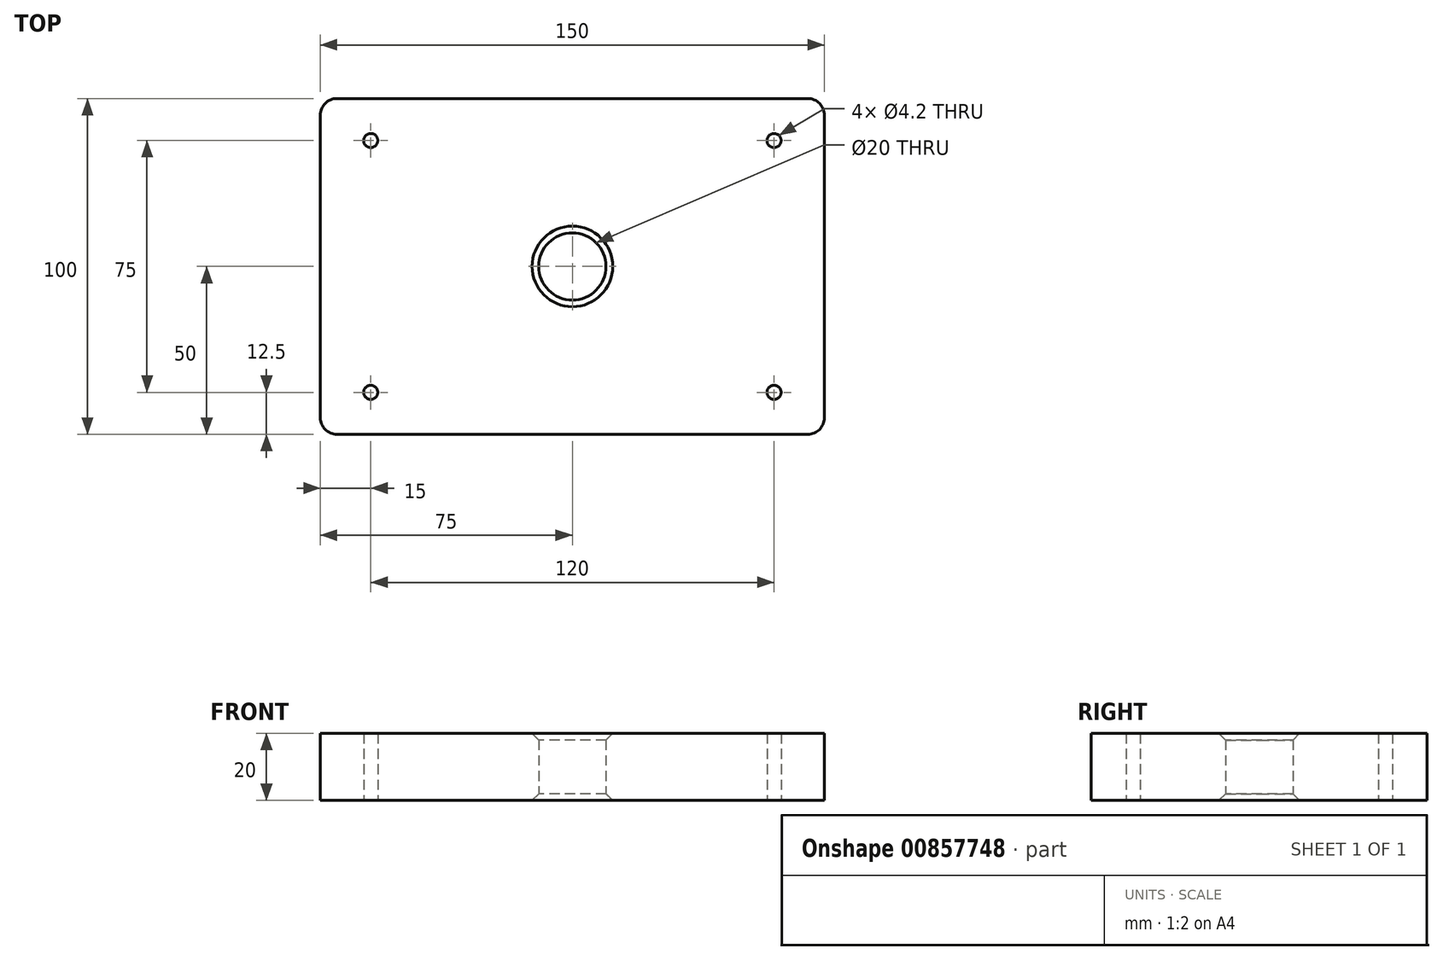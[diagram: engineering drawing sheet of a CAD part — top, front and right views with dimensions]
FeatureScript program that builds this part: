
annotation { "Feature Type Name" : "Feature", "Feature Type Description" : "" }
export const myFeature = defineFeature(function(context is Context, id is Id, definition is map)
    precondition{}
    {
        {
            var Q0;
            Q0=qCreatedBy(makeId("Top.planeOp"),FACE);
            var sketch = newSketch(context, id + "F0", { "sketchPlane" : qUnion([Q0])});
            skCircle(sketch, "E0", {"center": v(0, 0) * mm, "radius": 10 * mm});
            skLineSegment(sketch, "E1.bottom", {"start": v(-75, 50) * mm, "end": v(75, 50) * mm});
            skLineSegment(sketch, "E1.top", {"start": v(-75, -50) * mm, "end": v(75, -50) * mm});
            skLineSegment(sketch, "E1.left", {"start": v(-75, 50) * mm, "end": v(-75, -50) * mm});
            skLineSegment(sketch, "E1.right", {"start": v(75, 50) * mm, "end": v(75, -50) * mm});
            skLineSegment(sketch, "E2", {"start": v(-75, 50) * mm, "end": v(75, -50) * mm, "construction": true});
            skSolve(sketch);
        }
        {
            var Q0;
            Q0 = qSketchRegion(id + "F0", true);
            extrude(context, id + "F1", {"entities" : qUnion([Q0]), "depth" : 20 * mm, "offsetDistance" : 25.4 * mm});
        }
        {
            var Q0;
            Q0=makeQuery(id+"F1.opExtrude","SWEPT_EDGE",EDGE,{"disambiguationData":[OSD([sQuery(id+"F0.wireOp",EDGE,"E1.top"),sQuery(id+"F0.wireOp",EDGE,"E1.left")])]});
            var Q1;
            Q1=makeQuery(id+"F1.opExtrude","SWEPT_EDGE",EDGE,{"disambiguationData":[OSD([sQuery(id+"F0.wireOp",EDGE,"E1.bottom"),sQuery(id+"F0.wireOp",EDGE,"E1.left")])]});
            var Q2;
            Q2=makeQuery(id+"F1.opExtrude","SWEPT_EDGE",EDGE,{"disambiguationData":[OSD([sQuery(id+"F0.wireOp",EDGE,"E1.top"),sQuery(id+"F0.wireOp",EDGE,"E1.right")])]});
            var Q3;
            Q3=makeQuery(id+"F1.opExtrude","SWEPT_EDGE",EDGE,{"disambiguationData":[OSD([sQuery(id+"F0.wireOp",EDGE,"E1.bottom"),sQuery(id+"F0.wireOp",EDGE,"E1.right")])]});
            fillet(context, id + "F2", {"entities" : qUnion([Q0, Q1, Q2, Q3]), "radius" : 5 * mm, "tangentPropagation" : true, "allowEdgeOverflow" : false});
        }
        {
            var Q0;
            Q0=makeQuery(id+"F1.opExtrude","CAP_EDGE",EDGE,{"disambiguationData":[OSD([sQuery(id+"F0.wireOp",EDGE,"E0")])],"isStart":true});
            var Q1;
            Q1=makeQuery(id+"F1.opExtrude","CAP_EDGE",EDGE,{"disambiguationData":[OSD([sQuery(id+"F0.wireOp",EDGE,"E0")])],"isStart":false});
            chamfer(context, id + "F3", {"entities" : qUnion([Q0, Q1]), "width" : 2 * mm, "tangentPropagation" : true});
        }
        {
            var Q0;
            Q0=makeQuery(id+"F1.opExtrude","CAP_FACE",FACE,{"disambiguationData":[OSD([sQuery(id+"F0.wireOp",EDGE,"E0"),sQuery(id+"F0.wireOp",EDGE,"E1.bottom"),sQuery(id+"F0.wireOp",EDGE,"E1.top"),sQuery(id+"F0.wireOp",EDGE,"E1.left"),sQuery(id+"F0.wireOp",EDGE,"E1.right")])],"isStart":true});
            var sketch = newSketch(context, id + "F4", { "sketchPlane" : qUnion([Q0])});
            skPoint(sketch, "E3", {"position": v(60, -37.5) * mm});
            skPoint(sketch, "E4", {"position": v(-60, -37.5) * mm});
            skPoint(sketch, "E5", {"position": v(-60, 37.5) * mm});
            skPoint(sketch, "E6", {"position": v(60, 37.5) * mm});
            skLineSegment(sketch, "E7.bottom", {"start": v(60, -37.5) * mm, "end": v(-60, -37.5) * mm});
            skLineSegment(sketch, "E7.top", {"start": v(60, 37.5) * mm, "end": v(-60, 37.5) * mm});
            skLineSegment(sketch, "E7.left", {"start": v(60, -37.5) * mm, "end": v(60, 37.5) * mm});
            skLineSegment(sketch, "E7.right", {"start": v(-60, -37.5) * mm, "end": v(-60, 37.5) * mm});
            skLineSegment(sketch, "E8", {"start": v(-60, 37.5) * mm, "end": v(60, -37.5) * mm, "construction": true});
            skSolve(sketch);
        }
        {
            var Q0;
            Q0=sQuery(id+"F4.wireOp",VERTEX,"E3");
            var Q1;
            Q1=sQuery(id+"F4.wireOp",VERTEX,"E4");
            var Q2;
            Q2=sQuery(id+"F4.wireOp",VERTEX,"E5");
            var Q3;
            Q3=sQuery(id+"F4.wireOp",VERTEX,"E6");
            var Q4;
            Q4=makeQuery(id+"F1.opExtrude","SWEPT_BODY",BODY,{"disambiguationData":[OSD([sQuery(id+"F0.wireOp",EDGE,"E0"),sQuery(id+"F0.wireOp",EDGE,"E1.bottom"),sQuery(id+"F0.wireOp",EDGE,"E1.top"),sQuery(id+"F0.wireOp",EDGE,"E1.left"),sQuery(id+"F0.wireOp",EDGE,"E1.right")])]});
            hole(context, id + "F5", {"style" : HoleStyle.SIMPLE, "endStyle" : HoleEndStyle.THROUGH, "standardTappedOrClearance" : lookupTablePath({ "standard" : "ISO", "engagement" : "75%", "pitch" : "0.8 mm", "size" : "M5", "type" : "Tapped" }), "standardBlindInLast" : lookupTablePath({ "standard" : "ISO", "engagement" : "75%", "pitch" : "0.8 mm", "size" : "M5", "type" : "Tapped" }), "holeDiameter" : 4.2 * mm, "majorDiameter" : 5 * mm, "showTappedDepth" : true, "isTappedThrough" : true, "tappedDepth" : 12.7 * mm, "tapClearance" : 3, "locations" : qUnion([Q0, Q1, Q2, Q3]), "scope" : qUnion([Q4])});
        }
    });
